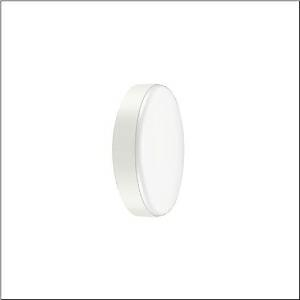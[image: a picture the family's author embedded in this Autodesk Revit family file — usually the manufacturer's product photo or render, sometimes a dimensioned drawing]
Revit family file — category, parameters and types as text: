
# Revit family: rondel_31_51wc10ma32as
name_source: partatom
category: Lighting Fixtures
units: mm (PartAtom-declared; Revit-internal decimal feet)

## family parameters
Cut with Voids When Loaded = No
Host = Face
Light Source = No
Part Type = Normal
Room Calculation Point = No
Round Connector Dimension = Use Diameter
Shared = No

## types (1)
- --- (1 x LED, 2450 lm, 20.4 W, 3000K)
    Apparent Load = 20 VA
    CIE Flux Codes = 44 75 94 94 100
    Color Rendering = 80
    Color Temperature = 3000K
    Default Elevation = 1800 mm
    Description = Rondel 31, wall and ceiling luminaire, primary optical cover: cover, of PC, opal, light emission: direct distribution, primary light characteristic: symmetric, installation type: surface-mounted, LED, rated luminous flux: 2.300lm, luminous efficacy: 112lm/W, light colour: 830, colour temperature: 3000K, with terminal, 3-pole, max. 2.5mm², mains connection: 220..240V, AC, 50/60Hz, rated input power: 20.5W, luminaire housing, of PC, traffic white (RAL 9016), diameter: 350mm, brightness and presence sensor, HF sensor, protection rating (complete): IP65, insulation class (complete): insulation class II (safety insulation), certification: CE, impact resistance: IK10, permissible storage temperature: -20..+60°C, packaging unit: 1 piece
    Height = 97 mm
    Lamp = 1 x LED
    Lamp Light Flux = 2450 lm
    Lamp Power = 20.4 W
    Lamp count = 1
    Length = 350 mm
    Luminous efficacy = 120 lm/W
    Manufacturer = Siteco
    ModVariant = No
    Model = 51WC10MA32AS
    Mounting Place = Ceiling
    Mounting Type = Surface mounted
    Number of Poles = 1
    OnlyDefault = Yes
    Power Factor = 1
    Product Name = Rondel 31
    Product group = wall and ceiling luminaire
    ProductGroupID = 301
    Protection Class = Protection class II
    Protection Degree = IP 65
    RLX_Detail_Level = 1
    RlxData = <blob elided: 30353 chars, md5=cd8cbbe6>
    Socket = socket
    Standby Power = 0 W
    System Light Flux = 2450 lm
    System Power = 20 W
    Type Comments = factory setting: luminous flux: 100 % | (ON | ON)
    Type Image = l_1007027.jpg
    URL = http://relux.com
    VarID = @adj_020229
    Voltage = 0 V
    Weight = 0.00 kg
    Width = 0 mm  [stored 0 ft]

note: [stored X ft] marks values corroborated as IEEE doubles in the binary element streams (Revit-internal decimal feet)

## geometry (parser evidence)
native form markers: Blend x4, Sweep x14
no freeform markers — native parametric forms only
